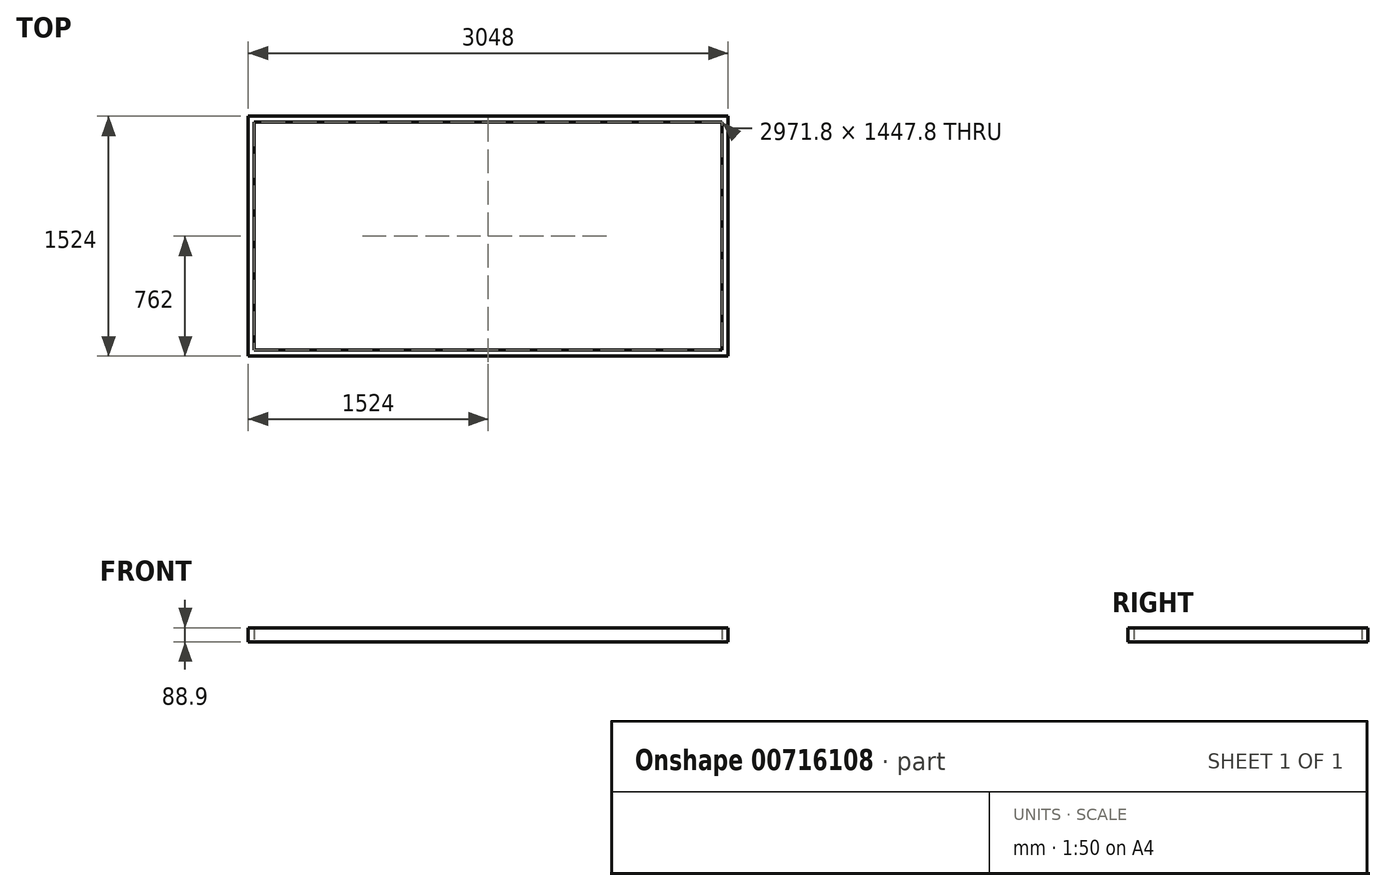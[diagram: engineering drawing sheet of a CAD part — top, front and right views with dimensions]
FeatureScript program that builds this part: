
annotation { "Feature Type Name" : "Feature", "Feature Type Description" : "" }
export const myFeature = defineFeature(function(context is Context, id is Id, definition is map)
    precondition{}
    {
        {
            var Q0;
            Q0=qCreatedBy(makeId("Top.planeOp"),FACE);
            var sketch = newSketch(context, id + "F0", { "sketchPlane" : qUnion([Q0])});
            skLineSegment(sketch, "E0.bottom", {"start": v(1524, 762) * mm, "end": v(-1524, 762) * mm});
            skLineSegment(sketch, "E0.top", {"start": v(1524, -762) * mm, "end": v(-1524, -762) * mm});
            skLineSegment(sketch, "E0.left", {"start": v(1524, 762) * mm, "end": v(1524, -762) * mm});
            skLineSegment(sketch, "E0.right", {"start": v(-1524, 762) * mm, "end": v(-1524, -762) * mm});
            skPoint(sketch, "E0.middle", {"position": v(0, 0) * mm});
            skLineSegment(sketch, "E1.bottom", {"start": v(1485.9, 723.9) * mm, "end": v(-1485.9, 723.9) * mm});
            skLineSegment(sketch, "E1.top", {"start": v(1485.9, -723.9) * mm, "end": v(-1485.9, -723.9) * mm});
            skLineSegment(sketch, "E1.left", {"start": v(1485.9, 723.9) * mm, "end": v(1485.9, -723.9) * mm});
            skLineSegment(sketch, "E1.right", {"start": v(-1485.9, 723.9) * mm, "end": v(-1485.9, -723.9) * mm});
            skSolve(sketch);
        }
        {
            var Q0;
            Q0=makeQuery(id+"F0.imprint","IMPRINT",FACE,{"disambiguationData":[TD([[makeQuery(id+"F0.imprint","IMPRINT",EDGE,{"derivedFrom":sQuery(id+"F0.wireOp",EDGE,"E0.bottom")}),1.0]])]});
            extrude(context, id + "F1", {"entities" : qUnion([Q0]), "depth" : 88.9 * mm, "offsetDistance" : 25.4 * mm});
        }
    });
